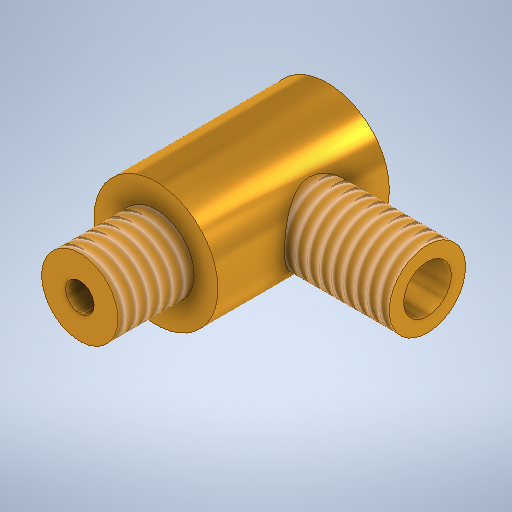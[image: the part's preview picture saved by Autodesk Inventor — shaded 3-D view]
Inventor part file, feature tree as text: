
AUTODESK INVENTOR PART (.ipt)
format: ipt  version: 2025.1 (Build 291241000, 241)  size: 365,568 bytes
history: native  units: mm
features: sketch x4, thread x2, hole x2, revolve x1, plane x1, extrude x1
ambient origin geometry x8: Origin, YZ Plane, XZ Plane, XY Plane, X Axis, Y Axis, Z Axis, Center Point
bodies: Solid1 (feature_tree)
feature tree (11):
  revolve  "Revolution1"  [1 undecoded]
  thread  "Thread1"  [1 undecoded]
  plane  "Work Plane1"
  extrude  "Extrusion1"  TaperAngle=90.0deg  [1 undecoded]
  hole  "Hole1"  [1 undecoded]
  hole  "Hole2"  [1 undecoded]
  thread  "Thread2"  [1 undecoded]
  sketch  "Sketch1"  dims[d0=13.0mm d1=8.0mm d2=8.0mm]
  sketch  "Sketch2"  dims[d3=18.0mm d4=90.0deg]
  sketch  "Sketch3"  dims[d5=8.0mm d6=0.0mm d7=17.5mm]
  sketch  "Sketch4"  dims[d8=8.0mm d9=7.0mm d10=10.0mm d11=0.0mm d12=4.0mm d13=6.0mm d14=5.0mm d15=10.0mm d16=90.0deg d17=7.5mm d18=0.0mm d19=3.0mm d20=6.0mm d21=4.0mm d22=2.0mm d23=90.0deg d24=20.0mm d25=0.0mm d26=15.0mm d27=0.0mm]
note: 6 required parameter values undecoded (feature->parameter linkage not recoverable at this tier; creation-order binding heuristic only, values carry confidence <= 0.55)